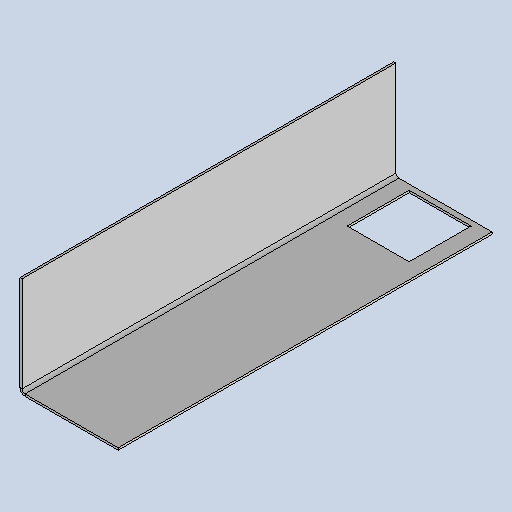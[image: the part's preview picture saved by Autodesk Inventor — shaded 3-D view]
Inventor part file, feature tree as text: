
AUTODESK INVENTOR PART (.ipt)
format: ipt  version: 2025.1 (Build 291241020, 241B)  size: 165,376 bytes
history: native  units: mm
features: sheet_metal_op x4, other x4, sketch x3
ambient origin geometry x8: Origin, YZ Plane, XZ Plane, XY Plane, X Axis, Y Axis, Z Axis, Center Point
bodies: Body1 (feature_tree)
feature tree (11):
  sheet_metal_op  "Face3"
  sheet_metal_op  "Flange3"
  sketch  "Sketch1"  dims[d154=92.0mm]
  other  "Plate5"
  sketch  "Sketch7"  dims[d155=350.0mm]
  other  "Plate6"
  sheet_metal_op  "Bend3"
  sheet_metal_op  "Corner3"
  sketch  "Sketch8"  dims[d156=2.0mm d157=2.0mm d158=1.0mm d159=4.0mm d160=2.75mm d161=94.0mm d162=90.0deg d163=2.75mm d164=8.0mm d165=2.0mm d166=2.75mm d167=58.0mm d168=58.0mm d169=5.0mm d170=2.0mm d171=0.0mm]
  other  "Cut1"
  other  "Definition1"
